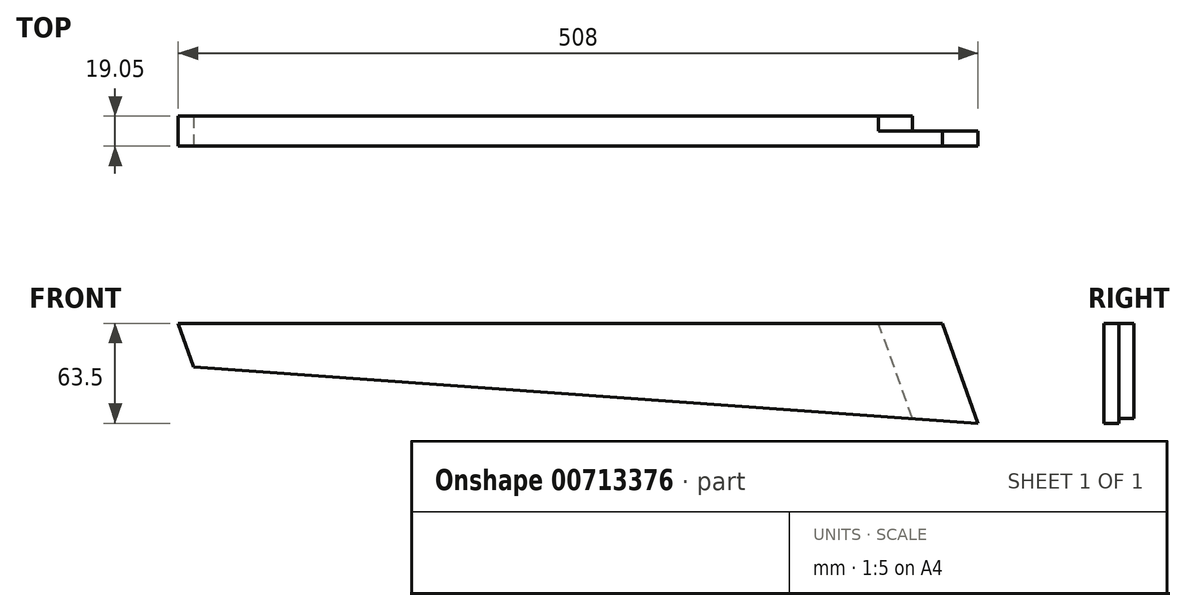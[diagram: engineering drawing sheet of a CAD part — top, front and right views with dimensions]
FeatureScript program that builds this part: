
annotation { "Feature Type Name" : "Feature", "Feature Type Description" : "" }
export const myFeature = defineFeature(function(context is Context, id is Id, definition is map)
    precondition{}
    {
        {
            var Q0;
            Q0=qCreatedBy(makeId("Front.planeOp"),FACE);
            var sketch = newSketch(context, id + "F0", { "sketchPlane" : qUnion([Q0])});
            skLineSegment(sketch, "E0.bottom", {"start": v(261.04, 0) * mm, "end": v(-246.96, 0) * mm});
            skLineSegment(sketch, "E0.top", {"start": v(261.04, 63.5) * mm, "end": v(-246.96, 63.5) * mm});
            skLineSegment(sketch, "E0.left", {"start": v(261.04, 0) * mm, "end": v(261.04, 63.5) * mm});
            skLineSegment(sketch, "E0.right", {"start": v(-246.96, 0) * mm, "end": v(-246.96, 63.5) * mm});
            skSolve(sketch);
        }
        {
            var Q0;
            Q0 = qSketchRegion(id + "F0", true);
            extrude(context, id + "F1", {"entities" : qUnion([Q0]), "depth" : 19.05 * mm, "offsetDistance" : 25.4 * mm});
        }
        {
            var Q0;
            Q0=makeQuery(id+"F1.opExtrude","CAP_FACE",FACE,{"disambiguationData":[OSD([sQuery(id+"F0.wireOp",EDGE,"E0.bottom"),sQuery(id+"F0.wireOp",EDGE,"E0.top"),sQuery(id+"F0.wireOp",EDGE,"E0.left"),sQuery(id+"F0.wireOp",EDGE,"E0.right")])],"isStart":false});
            var sketch = newSketch(context, id + "F2", { "sketchPlane" : qUnion([Q0])});
            skLineSegment(sketch, "E1", {"start": v(-246.96, 63.5) * mm, "end": v(-224.26, 0) * mm});
            skLineSegment(sketch, "E2", {"start": v(-224.26, 0) * mm, "end": v(-246.96, 0) * mm});
            skLineSegment(sketch, "E3", {"start": v(-246.96, 0) * mm, "end": v(-246.96, 63.5) * mm});
            skSolve(sketch);
        }
        {
            var Q0;
            Q0 = qSketchRegion(id + "F2", true);
            extrude(context, id + "F3", {"entities" : qUnion([Q0]), "operationType" : NewBodyOperationType.REMOVE, "oppositeDirection" : true, "depth" : 50.8 * mm, "offsetDistance" : 25.4 * mm});
        }
        {
            var Q0;
            Q0=makeQuery(id+"F1.opExtrude","CAP_FACE",FACE,{"disambiguationData":[OSD([sQuery(id+"F0.wireOp",EDGE,"E0.bottom"),sQuery(id+"F0.wireOp",EDGE,"E0.top"),sQuery(id+"F0.wireOp",EDGE,"E0.left"),sQuery(id+"F0.wireOp",EDGE,"E0.right")])],"isStart":false});
            var sketch = newSketch(context, id + "F4", { "sketchPlane" : qUnion([Q0])});
            skLineSegment(sketch, "E4", {"start": v(-237.09, 35.88) * mm, "end": v(261.04, 0) * mm});
            skLineSegment(sketch, "E5", {"start": v(261.04, 0) * mm, "end": v(-224.26, 0) * mm});
            skLineSegment(sketch, "E6", {"start": v(-224.26, 0) * mm, "end": v(-237.09, 35.88) * mm});
            skSolve(sketch);
        }
        {
            var Q0;
            Q0 = qSketchRegion(id + "F4", true);
            extrude(context, id + "F5", {"entities" : qUnion([Q0]), "operationType" : NewBodyOperationType.REMOVE, "oppositeDirection" : true, "depth" : 50.8 * mm, "offsetDistance" : 25.4 * mm});
        }
        {
            var Q0;
            Q0=makeQuery(id+"F1.opExtrude","CAP_FACE",FACE,{"disambiguationData":[OSD([sQuery(id+"F0.wireOp",EDGE,"E0.bottom"),sQuery(id+"F0.wireOp",EDGE,"E0.top"),sQuery(id+"F0.wireOp",EDGE,"E0.left"),sQuery(id+"F0.wireOp",EDGE,"E0.right")])],"isStart":false});
            var sketch = newSketch(context, id + "F6", { "sketchPlane" : qUnion([Q0])});
            skLineSegment(sketch, "E7", {"start": v(261.04, 0) * mm, "end": v(238.33, 63.5) * mm});
            skLineSegment(sketch, "E8", {"start": v(238.33, 63.5) * mm, "end": v(261.04, 63.5) * mm});
            skLineSegment(sketch, "E9", {"start": v(261.04, 63.5) * mm, "end": v(261.04, 0) * mm});
            skSolve(sketch);
        }
        {
            var Q0;
            Q0 = qSketchRegion(id + "F6", true);
            extrude(context, id + "F7", {"entities" : qUnion([Q0]), "operationType" : NewBodyOperationType.REMOVE, "oppositeDirection" : true, "depth" : 38.1 * mm, "offsetDistance" : 25.4 * mm});
        }
        {
            var Q0;
            Q0=makeQuery(id+"F7.boolean.opBoolean","COPY",FACE,{"derivedFrom":makeQuery(id+"F7.opExtrude","SWEPT_FACE",FACE,{"disambiguationData":[OSD([sQuery(id+"F6.wireOp",EDGE,"E7")])]})});
            var sketch = newSketch(context, id + "F8", { "sketchPlane" : qUnion([Q0])});
            skLineSegment(sketch, "E10", {"start": v(-9.53, -87.89) * mm, "end": v(0, -87.89) * mm});
            skLineSegment(sketch, "E11", {"start": v(0, -87.89) * mm, "end": v(0, 40.52) * mm});
            skLineSegment(sketch, "E12", {"start": v(-9.53, 4.15) * mm, "end": v(0, 40.52) * mm});
            skLineSegment(sketch, "E13", {"start": v(-9.53, -87.89) * mm, "end": v(-9.53, 4.15) * mm});
            skSolve(sketch);
        }
        {
            var Q0;
            Q0 = qSketchRegion(id + "F8", true);
            extrude(context, id + "F9", {"entities" : qUnion([Q0]), "operationType" : NewBodyOperationType.REMOVE, "oppositeDirection" : true, "depth" : 38.1 * mm, "offsetDistance" : 25.4 * mm});
        }
    });
